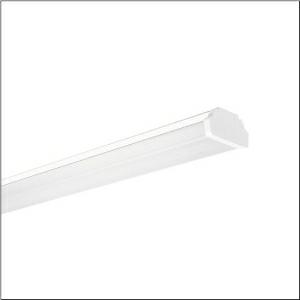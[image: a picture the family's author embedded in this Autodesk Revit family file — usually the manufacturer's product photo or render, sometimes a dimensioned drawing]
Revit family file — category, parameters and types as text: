
# Revit family: dus_31_gen_2_53bd812dv6dxd2_193c
name_source: partatom
category: Lighting Fixtures
units: mm (PartAtom-declared; Revit-internal decimal feet)

## family parameters
Cut with Voids When Loaded = No
Host = Face
Light Source = No
Part Type = Normal
Room Calculation Point = No
Round Connector Dimension = Use Diameter
Shared = No

## types (1)
- --- (1 x LED, 13280 lm, 74.9 W, 6500K)
    Apparent Load = 75 VA
    CIE Flux Codes = 47 80 95 93 100
    Color Rendering = 80
    Color Temperature = 6500K
    Default Elevation = 1800 mm
    Description = DUS 31 Gen.2, luminaire insert, of sheet steel, coil coated, white, length: 1.535mm, width: 81mm, height: 90mm, 5x system unit, system units: 307mm, LED rated luminous flux: 13.280lm, light colour: 865, SDCM (Standard Deviation of Colour Matching)MacAdam ≤ 3 SDCM (initial), control gear: DALI 2, control gear: ECG DALI, with plug, 5-pole, with phase selection, mains connection: 220..240V, AC, 50/60Hz, rated input power: 75W, through-wiring accessed according to module size, primary optical cover: cover, of PMMA, light emission: direct distribution, primary light characteristic: symmetric, protection rating (complete): IP20, protection rating (LED compartment): IP50, insulation class (complete): insulation class I (protective earthing), certification: CE, ENEC, VDE, UKCA, impact resistance: IK03, permissible ambient temperature for indoor applications: -25..+35°C, corresponds to IFS (International Featured Standards) requirements for safety and quality in the food industry, reducing of maximum allowable ambient temperature of 5°C with ceiling mounting, packaging unit: 1 piece
    Height = 95 mm
    Lamp = 1 x LED
    Lamp Light Flux = 13280 lm
    Lamp Power = 74.9 W
    Lamp count = 1
    Length = 1535 mm
    Luminous efficacy = 177 lm/W
    Manufacturer = Siteco
    ModVariant = No
    Model = 53BD812DV6DXD2
    Mounting Place = Ceiling
    Mounting Type = Pendant
    Number of Poles = 1
    OnlyDefault = Yes
    Power Factor = 1
    Product Name = DUS 31 Gen.2
    Product group = luminaire insert | ceiling pendant
    ProductGroupID = 901
    Protection Class = Protection class I
    Protection Degree = IP 20
    RLX_Detail_Level = 1
    RLX_Emergency_Light_Flux = 0 lm
    RLX_Emergency_Type = 0
    RLX_Emergency_Type_DB = No
    RlxData = <blob elided: 32233 chars, md5=74deb650>
    Socket = socket
    Standby Power = 0 W
    System Light Flux = 13280 lm
    System Power = 75 W
    Type Comments = factory setting: luminous flux: 100 % | dim-lin: 254 | 511 mA
    Type Image = l_1319596.jpg
    URL = http://relux.com
    VarID = @adj_049743
    Voltage = 0 V
    Weight = 0.00 kg
    Width = 81 mm

## geometry (parser evidence)
native form markers: Blend x4, Sweep x14
no freeform markers — native parametric forms only
